# Revit family: FU_Modular_Sandler_Escala_Frames
name_source: partatom
category: Furniture
units: mm (PartAtom-declared; Revit-internal decimal feet)

## family parameters
Always vertical = Yes
Cut with Voids When Loaded = No
OmniClass Number = 23.40.20.00
OmniClass Title = General Furniture and Specialties
Room Calculation Point = No
Shared = No
Work Plane-Based = No

## types (8) — shared parameters
Depth = 800 mm  [stored 2.62467 ft]
Height = 260 mm  [stored 0.853018 ft]
Manufacturer = Sandler
URL = https://www.sandlerseating.com
zero-valued in all types: Default Elevation

## per-type parameters (varying)
| type | Description | IsVisible | Width |
| ESCALAS 0025 | Epoxy coated frame for Sofa – 200x80cm | No | 2000 mm  [stored 6.56168 ft] |
| ESCALAS 0020 | Epoxy coated frame for Sofa – 160x80cm | No | 1600 mm  [stored 5.24934 ft] |
| ESCALAS 0010 | Epoxy coated frame for Sofa – 80x80cm | No | 800 mm  [stored 2.62467 ft] |
| ESCALAS 0015 | Epoxy coated frame for Sofa – 120x80cm | No | 1200 mm |
| ESCALAS 0030 | Epoxy coated frame for Sofa – 240x80cm | No | 2400 mm |
| ESCALAS 0035 | Epoxy coated frame for Sofa – 280x80cm | No | 2800 mm  [stored 9.18635 ft] |
| ESCALAS 0040 | Epoxy coated frame for Sofa – 320x80cm | Yes | 3200 mm  [stored 10.4987 ft] |
| ESCALAS 0045 | Epoxy coated frame for Sofa – 360x80cm | Yes | 3600 mm  [stored 11.811 ft] |

note: column(s) folded — value = type name in every type: Model

note: [stored X ft] marks values corroborated as IEEE doubles in the binary element streams (Revit-internal decimal feet)

## geometry (parser evidence)
native form markers: Sweep x3
no freeform markers — native parametric forms only
